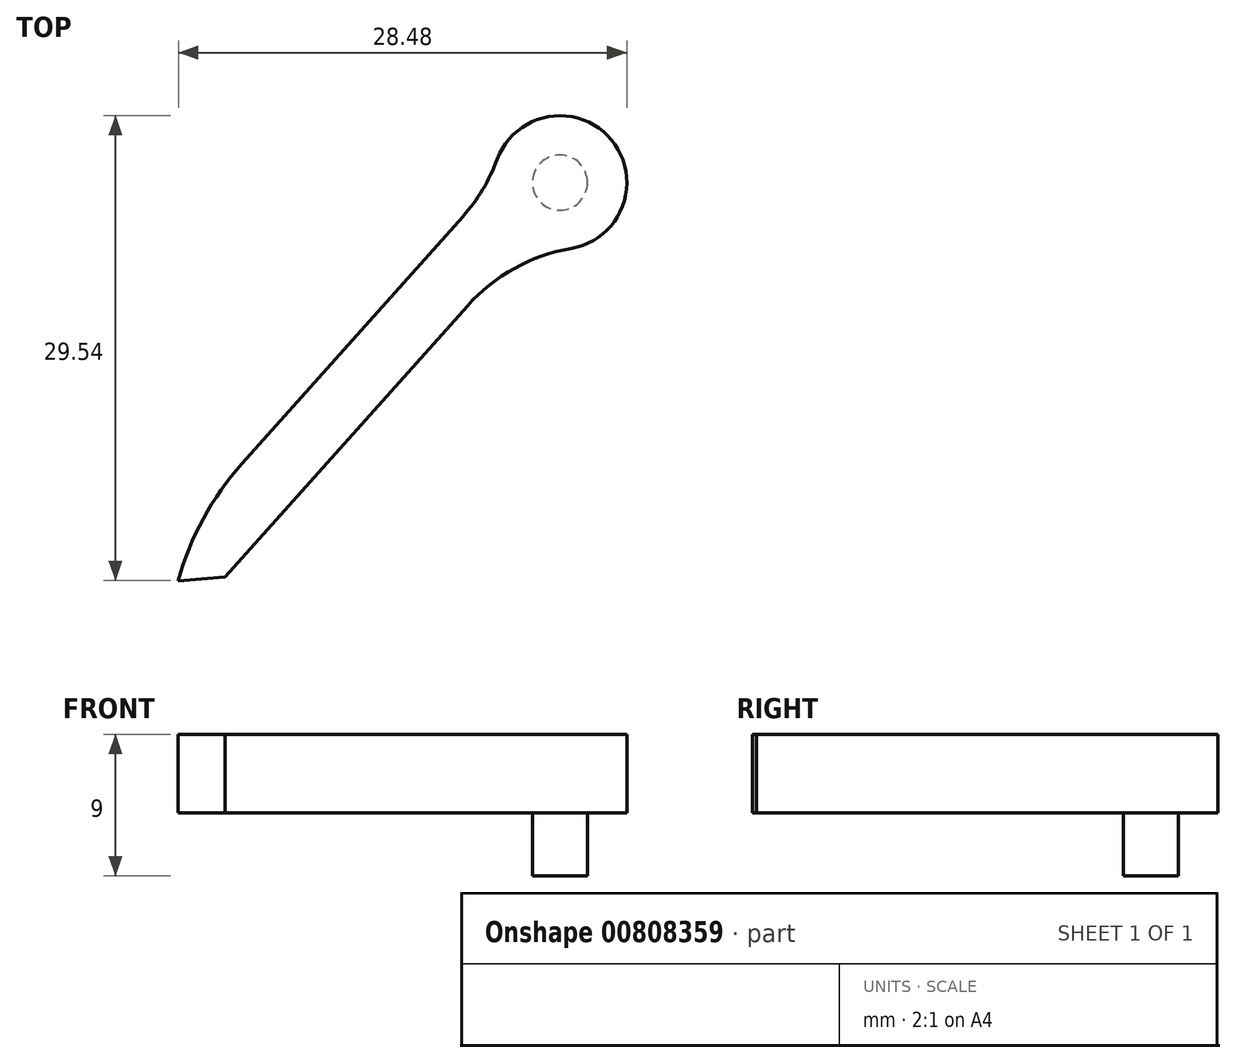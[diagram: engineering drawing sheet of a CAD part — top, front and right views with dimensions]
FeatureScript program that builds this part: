
annotation { "Feature Type Name" : "Feature", "Feature Type Description" : "" }
export const myFeature = defineFeature(function(context is Context, id is Id, definition is map)
    precondition{}
    {
        {
            var Q0;
            Q0=qCreatedBy(makeId("Top.planeOp"),FACE);
            var sketch = newSketch(context, id + "F0", { "sketchPlane" : qUnion([Q0])});
            skCircle(sketch, "E0", {"center": v(-0.4, 8.92) * mm, "radius": 4.25 * mm});
            skPoint(sketch, "E0.centerSnap0", {"position": v(-3.4, 8.92) * mm});
            skLineSegment(sketch, "E1", {"start": v(-4.66, 8.92) * mm, "end": v(-24.64, -13.46) * mm});
            skLineSegment(sketch, "E2", {"start": v(-24.64, -13.46) * mm, "end": v(-21.66, -16.12) * mm});
            skLineSegment(sketch, "E3", {"start": v(-21.66, -16.12) * mm, "end": v(-2.56, 5.25) * mm});
            skCircle(sketch, "E4", {"center": v(-0.4, 8.92) * mm, "radius": 1.75 * mm});
            skLineSegment(sketch, "E5", {"start": v(-24.64, -13.46) * mm, "end": v(-24.64, -16.12) * mm});
            skPoint(sketch, "E5.endSnap0", {"position": v(-25.45, -16.12) * mm});
            skLineSegment(sketch, "E6", {"start": v(-21.66, -16.12) * mm, "end": v(-24.64, -16.37) * mm});
            skLineSegment(sketch, "E7", {"start": v(-24.64, -16.37) * mm, "end": v(-24.64, -16.12) * mm});
            skSolve(sketch);
        }
        {
            var Q0;
            Q0 = qSketchRegion(id + "F0", true);
            extrude(context, id + "F1", {"entities" : qUnion([Q0]), "depth" : 5 * mm, "offsetDistance" : 25 * mm});
        }
        {
            var Q0;
            Q0=makeQuery(id+"F0.imprint","IMPRINT",FACE,{"disambiguationData":[TD([[makeQuery(id+"F0.imprint","IMPRINT",EDGE,{"derivedFrom":sQuery(id+"F0.wireOp",EDGE,"E4")}),1.0]])]});
            extrude(context, id + "F2", {"entities" : qUnion([Q0]), "operationType" : NewBodyOperationType.ADD, "depth" : -4 * mm, "offsetDistance" : 25 * mm, "hasSecondDirection" : true, "secondDirectionOppositeDirection" : false, "secondDirectionDepth" : 5 * mm});
        }
        {
            var Q0;
            Q0=makeQuery(id+"F1.opExtrude","SWEPT_EDGE",EDGE,{"disambiguationData":[OSD([sQuery(id+"F0.wireOp",EDGE,"E1"),sQuery(id+"F0.wireOp",EDGE,"E2"),sQuery(id+"F0.wireOp",EDGE,"1de9a5ce-558e-4a68-92d8-88db7121e93d")])]});
            fillet(context, id + "F3", {"entities" : qUnion([Q0]), "radius" : 18.48 * mm, "tangentPropagation" : true, "allowEdgeOverflow" : false});
        }
        {
            var Q0;
            Q0=makeQuery(id+"F1.opExtrude","SWEPT_EDGE",EDGE,{"disambiguationData":[OSD([sQuery(id+"F0.wireOp",EDGE,"E0"),sQuery(id+"F0.wireOp",EDGE,"E3")])]});
            var Q1;
            Q1=makeQuery(id+"F1.opExtrude","SWEPT_EDGE",EDGE,{"disambiguationData":[OSD([sQuery(id+"F0.wireOp",EDGE,"E0"),sQuery(id+"F0.wireOp",EDGE,"E1")])]});
            fillet(context, id + "F4", {"entities" : qUnion([Q0, Q1]), "radius" : 11.37 * mm, "tangentPropagation" : true, "allowEdgeOverflow" : false});
        }
    });
